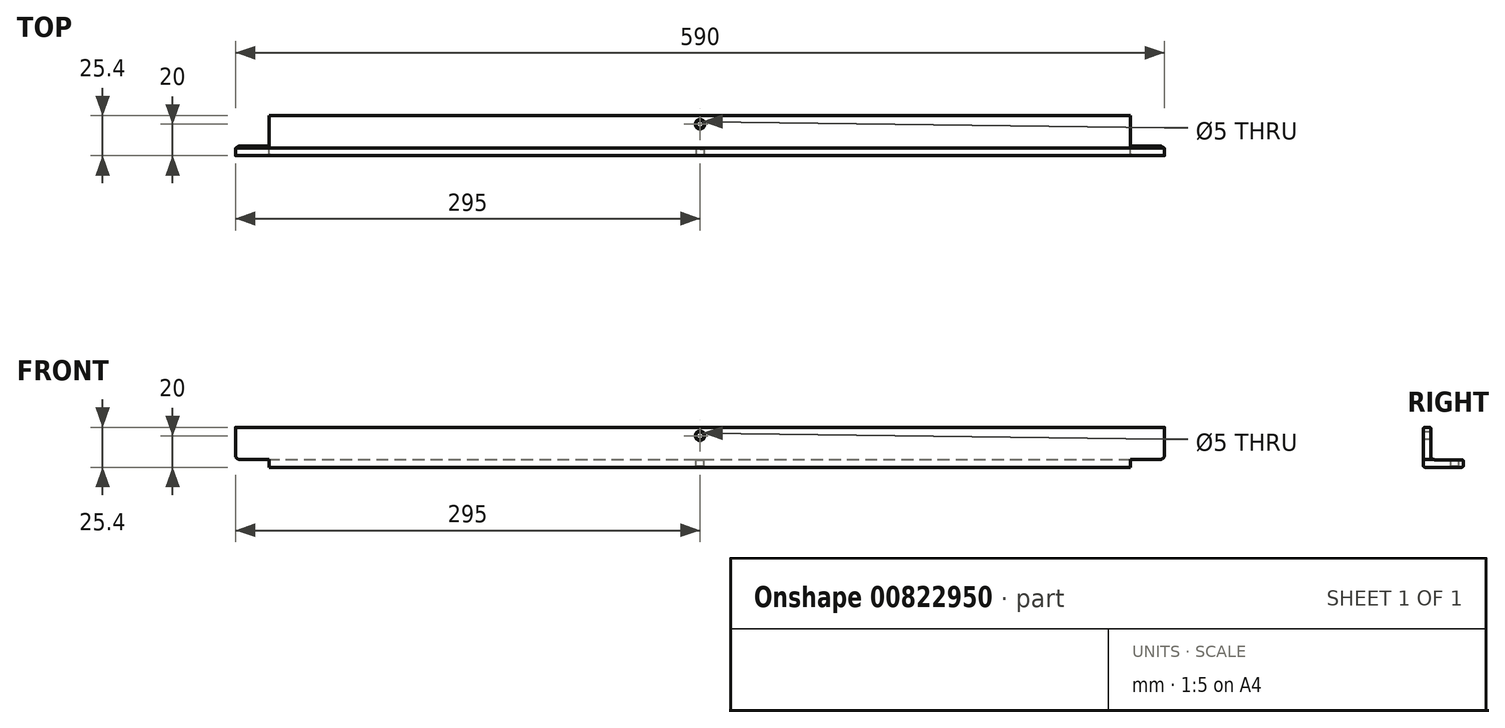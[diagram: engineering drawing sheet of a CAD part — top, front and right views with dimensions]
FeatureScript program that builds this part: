
annotation { "Feature Type Name" : "Feature", "Feature Type Description" : "" }
export const myFeature = defineFeature(function(context is Context, id is Id, definition is map)
    precondition{}
    {
        {
            var Q0;
            Q0=qCreatedBy(makeId("Right.planeOp"),FACE);
            var sketch = newSketch(context, id + "F0", { "sketchPlane" : qUnion([Q0])});
            skLineSegment(sketch, "E0", {"start": v(0, 0) * mm, "end": v(25.4, 0) * mm});
            skLineSegment(sketch, "E1", {"start": v(0, 0) * mm, "end": v(0, 25.4) * mm});
            skLineSegment(sketch, "E2", {"start": v(0, 25.4) * mm, "end": v(4.76, 25.4) * mm});
            skLineSegment(sketch, "E3", {"start": v(4.76, 25.4) * mm, "end": v(4.76, 4.76) * mm});
            skLineSegment(sketch, "E4", {"start": v(4.76, 4.76) * mm, "end": v(25.4, 4.76) * mm});
            skLineSegment(sketch, "E5", {"start": v(25.4, 4.76) * mm, "end": v(25.4, 0) * mm});
            skSolve(sketch);
        }
        {
            var Q0;
            Q0=qSketchRegion(id+"F0",true);
            extrude(context, id + "F1", {"entities" : qUnion([Q0]), "endBound" : BoundingType.SYMMETRIC, "depth" : 590 * mm, "offsetDistance" : 25 * mm});
        }
        {
            var Q0;
            Q0=makeQuery(id+"F1.opExtrude","SWEPT_EDGE",EDGE,{"disambiguationData":[OSD([sQuery(id+"F0.wireOp",EDGE,"E1"),sQuery(id+"F0.wireOp",EDGE,"E2")])]});
            var Q1;
            Q1=makeQuery(id+"F1.opExtrude","SWEPT_EDGE",EDGE,{"disambiguationData":[OSD([sQuery(id+"F0.wireOp",EDGE,"E2"),sQuery(id+"F0.wireOp",EDGE,"E3")])]});
            var Q2;
            Q2=makeQuery(id+"F1.opExtrude","SWEPT_EDGE",EDGE,{"disambiguationData":[OSD([sQuery(id+"F0.wireOp",EDGE,"E0"),sQuery(id+"F0.wireOp",EDGE,"E1")])]});
            var Q3;
            Q3=makeQuery(id+"F1.opExtrude","SWEPT_EDGE",EDGE,{"disambiguationData":[OSD([sQuery(id+"F0.wireOp",EDGE,"E4"),sQuery(id+"F0.wireOp",EDGE,"E5")])]});
            var Q4;
            Q4=makeQuery(id+"F1.opExtrude","SWEPT_EDGE",EDGE,{"disambiguationData":[OSD([sQuery(id+"F0.wireOp",EDGE,"E0"),sQuery(id+"F0.wireOp",EDGE,"E5")])]});
            fillet(context, id + "F2", {"entities" : qUnion([Q0, Q1, Q2, Q3, Q4]), "radius" : 1 * mm, "tangentPropagation" : true, "allowEdgeOverflow" : false});
        }
        {
            var Q0;
            Q0=makeQuery(id+"F1.opExtrude","SWEPT_EDGE",EDGE,{"disambiguationData":[OSD([sQuery(id+"F0.wireOp",EDGE,"E3"),sQuery(id+"F0.wireOp",EDGE,"E4")])]});
            fillet(context, id + "F3", {"entities" : qUnion([Q0]), "radius" : (3 * 25.4 / 16 / 2) * mm, "tangentPropagation" : true, "allowEdgeOverflow" : false});
        }
        {
            var Q0;
            Q0=makeQuery(id+"F1.opExtrude","SWEPT_FACE",FACE,{"disambiguationData":[OSD([sQuery(id+"F0.wireOp",EDGE,"E0")])]});
            var sketch = newSketch(context, id + "F4", { "sketchPlane" : qUnion([Q0])});
            skLineSegment(sketch, "E6.bottom", {"start": v(-323.5, -55) * mm, "end": v(-273.5, -55) * mm});
            skLineSegment(sketch, "E6.top", {"start": v(-323.5, -5) * mm, "end": v(-273.5, -5) * mm});
            skLineSegment(sketch, "E6.left", {"start": v(-323.5, -55) * mm, "end": v(-323.5, -5) * mm});
            skLineSegment(sketch, "E6.right", {"start": v(-273.5, -55) * mm, "end": v(-273.5, -5) * mm});
            skLineSegment(sketch, "E7", {"start": v(0, 0) * mm, "end": v(0, -138.54) * mm, "construction": true});
            skLineSegment(sketch, "E8.0", {"start": v(-295, 0) * mm, "end": v(295, 0) * mm, "construction": true});
            skLineSegment(sketch, "E9.0", {"start": v(-295, -1) * mm, "end": v(-295, -24.4) * mm, "construction": true});
            skLineSegment(sketch, "E10.MirrorCS", {"start": v(323.5, -5) * mm, "end": v(273.5, -5) * mm});
            skLineSegment(sketch, "E11.MirrorCS", {"start": v(323.5, -55) * mm, "end": v(323.5, -5) * mm});
            skLineSegment(sketch, "E12.MirrorCS", {"start": v(323.5, -55) * mm, "end": v(273.5, -55) * mm});
            skLineSegment(sketch, "E13.MirrorCS", {"start": v(273.5, -55) * mm, "end": v(273.5, -5) * mm});
            skSolve(sketch);
        }
        {
            var Q0;
            Q0=makeQuery(id+"F1.opExtrude","SWEPT_FACE",FACE,{"disambiguationData":[OSD([sQuery(id+"F0.wireOp",EDGE,"E3")])]});
            var sketch = newSketch(context, id + "F5", { "sketchPlane" : qUnion([Q0])});
            skLineSegment(sketch, "E14.bottom", {"start": v(-273.5, -45) * mm, "end": v(-323.5, -45) * mm});
            skLineSegment(sketch, "E14.top", {"start": v(-273.5, 5) * mm, "end": v(-323.5, 5) * mm});
            skLineSegment(sketch, "E14.left", {"start": v(-273.5, -45) * mm, "end": v(-273.5, 5) * mm});
            skLineSegment(sketch, "E14.right", {"start": v(-323.5, -45) * mm, "end": v(-323.5, 5) * mm});
            skLineSegment(sketch, "E15.0", {"start": v(-295, 25.4) * mm, "end": v(295, 25.4) * mm, "construction": true});
            skLineSegment(sketch, "E16.0", {"start": v(-295, 24.4) * mm, "end": v(-295, 7.14) * mm, "construction": true});
            skLineSegment(sketch, "E17", {"start": v(0, 0) * mm, "end": v(0, 107.54) * mm, "construction": true});
            skLineSegment(sketch, "E18.0", {"start": v(273.5, 0) * mm, "end": v(-273.5, 0) * mm, "construction": true});
            skLineSegment(sketch, "E19.MirrorCS", {"start": v(323.5, -45) * mm, "end": v(323.5, 5) * mm});
            skLineSegment(sketch, "E20.MirrorCS", {"start": v(273.5, -45) * mm, "end": v(273.5, 5) * mm});
            skLineSegment(sketch, "E21.MirrorCS", {"start": v(273.5, 5) * mm, "end": v(323.5, 5) * mm});
            skLineSegment(sketch, "E22.MirrorCS", {"start": v(273.5, -45) * mm, "end": v(323.5, -45) * mm});
            skSolve(sketch);
        }
        {
            var Q0;
            Q0 = qSketchRegion(id + "F5", true);
            extrude(context, id + "F6", {"entities" : qUnion([Q0]), "operationType" : NewBodyOperationType.REMOVE, "endBound" : BoundingType.SYMMETRIC, "oppositeDirection" : true, "depth" : 50 * mm, "offsetDistance" : 25 * mm});
        }
        {
            var Q0;
            Q0=makeQuery(id+"F6.boolean.opBoolean","INTERSECT",EDGE,{"derivedFrom":[makeQuery(id+"F1.opExtrude","CAP_FACE",FACE,{"disambiguationData":[OSD([sQuery(id+"F0.wireOp",EDGE,"E0"),sQuery(id+"F0.wireOp",EDGE,"E1"),sQuery(id+"F0.wireOp",EDGE,"E2"),sQuery(id+"F0.wireOp",EDGE,"E3"),sQuery(id+"F0.wireOp",EDGE,"E4"),sQuery(id+"F0.wireOp",EDGE,"E5")])],"isStart":false}),makeQuery(id+"F6.opExtrude","SWEPT_FACE",FACE,{"disambiguationData":[OSD([sQuery(id+"F5.wireOp",EDGE,"E14.top")])]})]});
            var Q1;
            Q1=makeQuery(id+"F6.boolean.opBoolean","INTERSECT",EDGE,{"derivedFrom":[makeQuery(id+"F1.opExtrude","CAP_FACE",FACE,{"disambiguationData":[OSD([sQuery(id+"F0.wireOp",EDGE,"E0"),sQuery(id+"F0.wireOp",EDGE,"E1"),sQuery(id+"F0.wireOp",EDGE,"E2"),sQuery(id+"F0.wireOp",EDGE,"E3"),sQuery(id+"F0.wireOp",EDGE,"E4"),sQuery(id+"F0.wireOp",EDGE,"E5")])],"isStart":true}),makeQuery(id+"F6.opExtrude","SWEPT_FACE",FACE,{"disambiguationData":[OSD([sQuery(id+"F5.wireOp",EDGE,"E21.MirrorCS")])]})]});
            fillet(context, id + "F7", {"entities" : qUnion([Q0, Q1]), "radius" : 2.5 * mm, "tangentPropagation" : true, "allowEdgeOverflow" : false});
        }
        {
            var Q0;
            Q0=makeQuery(id+"F1.opExtrude","SWEPT_FACE",FACE,{"disambiguationData":[OSD([sQuery(id+"F0.wireOp",EDGE,"E4")])]});
            var sketch = newSketch(context, id + "F8", { "sketchPlane" : qUnion([Q0])});
            skLineSegment(sketch, "E23", {"start": v(0, 0) * mm, "end": v(0, 20) * mm, "construction": true});
            skCircle(sketch, "E24", {"center": v(0, 20) * mm, "radius": 2.5 * mm});
            skSolve(sketch);
        }
        {
            var Q0;
            Q0 = qSketchRegion(id + "F8", true);
            extrude(context, id + "F9", {"entities" : qUnion([Q0]), "operationType" : NewBodyOperationType.REMOVE, "oppositeDirection" : true, "depth" : 25 * mm, "offsetDistance" : 25 * mm});
        }
        {
            var Q0;
            Q0=makeQuery(id+"F9.boolean.opBoolean","COPY",FACE,{"derivedFrom":makeQuery(id+"F9.opExtrude","SWEPT_FACE",FACE,{"disambiguationData":[OSD([sQuery(id+"F8.wireOp",EDGE,"E24")])]})});
            chamfer(context, id + "F10", {"entities" : qUnion([Q0]), "width" : 0.5 * mm, "tangentPropagation" : true});
        }
        {
            var Q0;
            Q0=makeQuery(id+"F1.opExtrude","SWEPT_FACE",FACE,{"disambiguationData":[OSD([sQuery(id+"F0.wireOp",EDGE,"E1")])]});
            var sketch = newSketch(context, id + "F11", { "sketchPlane" : qUnion([Q0])});
            skLineSegment(sketch, "E25", {"start": v(0, 0) * mm, "end": v(0, 20) * mm, "construction": true});
            skCircle(sketch, "E26", {"center": v(0, 20) * mm, "radius": 2.5 * mm});
            skSolve(sketch);
        }
        {
            var Q0;
            Q0 = qSketchRegion(id + "F11", true);
            extrude(context, id + "F12", {"entities" : qUnion([Q0]), "operationType" : NewBodyOperationType.REMOVE, "oppositeDirection" : true, "depth" : 25 * mm, "offsetDistance" : 25 * mm});
        }
        {
            var Q0;
            Q0=makeQuery(id+"F12.boolean.opBoolean","COPY",FACE,{"derivedFrom":makeQuery(id+"F12.opExtrude","SWEPT_FACE",FACE,{"disambiguationData":[OSD([sQuery(id+"F11.wireOp",EDGE,"E26")])]})});
            chamfer(context, id + "F13", {"entities" : qUnion([Q0]), "width" : 0.5 * mm, "tangentPropagation" : true});
        }
    });
